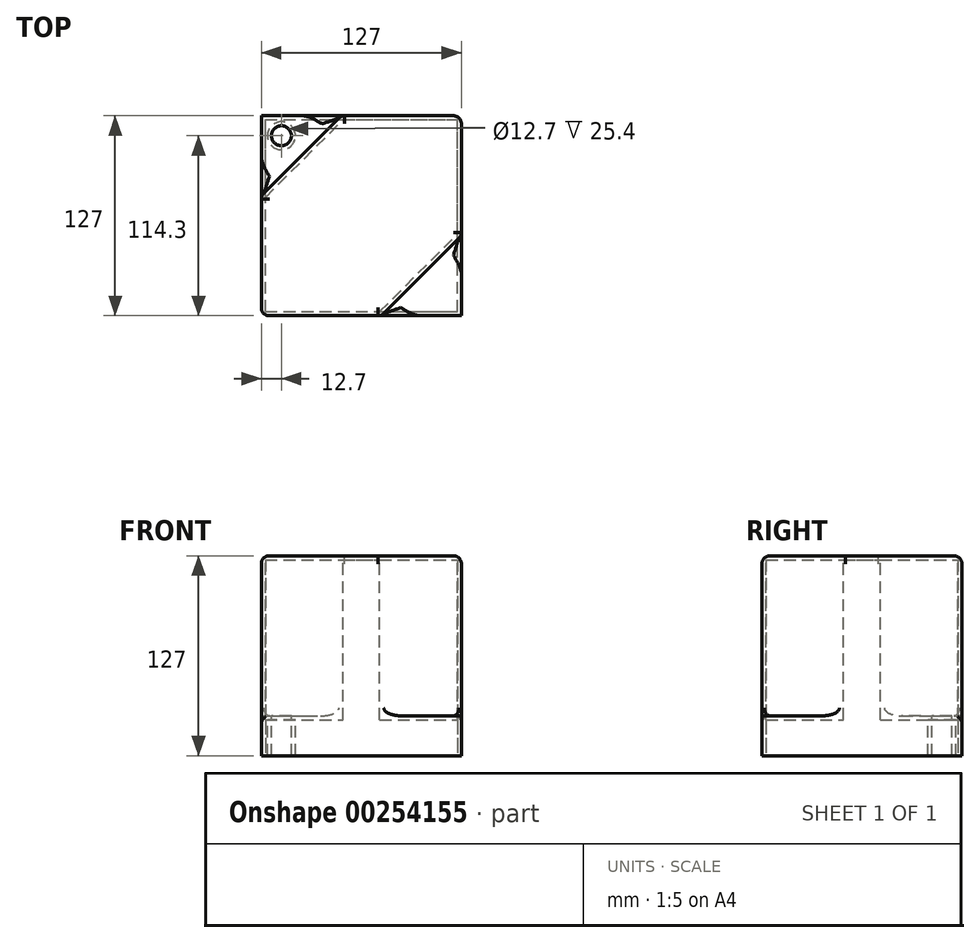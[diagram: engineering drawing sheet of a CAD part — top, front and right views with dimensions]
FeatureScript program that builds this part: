
annotation { "Feature Type Name" : "Feature", "Feature Type Description" : "" }
export const myFeature = defineFeature(function(context is Context, id is Id, definition is map)
    precondition{}
    {
        {
            var Q0;
            Q0=qCreatedBy(makeId("Top.planeOp"),FACE);
            var sketch = newSketch(context, id + "F0", { "sketchPlane" : qUnion([Q0])});
            skLineSegment(sketch, "E0.bottom", {"start": v(-63.5, -63.5) * mm, "end": v(63.5, -63.5) * mm});
            skLineSegment(sketch, "E0.top", {"start": v(-63.5, 63.5) * mm, "end": v(63.5, 63.5) * mm});
            skLineSegment(sketch, "E0.left", {"start": v(-63.5, -63.5) * mm, "end": v(-63.5, 63.5) * mm});
            skLineSegment(sketch, "E0.right", {"start": v(63.5, -63.5) * mm, "end": v(63.5, 63.5) * mm});
            skPoint(sketch, "E0.middle", {"position": v(0, 0) * mm});
            skLineSegment(sketch, "E1", {"start": v(63.5, 63.5) * mm, "end": v(-63.5, -63.5) * mm, "construction": true});
            skLineSegment(sketch, "E2", {"start": v(-63.5, 63.5) * mm, "end": v(-63.5, 12.7) * mm});
            skLineSegment(sketch, "E3", {"start": v(-12.7, 63.5) * mm, "end": v(-63.5, 63.5) * mm});
            skLineSegment(sketch, "E4.MirrorCS", {"start": v(63.5, -12.7) * mm, "end": v(63.5, -63.5) * mm});
            skLineSegment(sketch, "E5.MirrorCS", {"start": v(63.5, -63.5) * mm, "end": v(12.7, -63.5) * mm});
            skSolve(sketch);
        }
        {
            var Q0;
            Q0=makeQuery(id+"F0.imprint","IMPRINT",FACE,{"disambiguationData":[TD([[makeQuery(id+"F0.imprint","IMPRINT",EDGE,{"derivedFrom":sQuery(id+"F0.wireOp",EDGE,"E0.top")}),-1.0]])]});
            extrude(context, id + "F1", {"entities" : qUnion([Q0]), "depth" : 127 * mm});
        }
        {
            var Q0;
            Q0=makeQuery(id+"F1.opExtrude","CAP_FACE",FACE,{"disambiguationData":[OSD([sQuery(id+"F0.wireOp",EDGE,"E0.top"),sQuery(id+"F0.wireOp",EDGE,"E0.left"),sQuery(id+"F0.wireOp",EDGE,"E2"),sQuery(id+"F0.wireOp",EDGE,"E3"),sQuery(id+"F0.wireOp",EDGE,"E0.right"),sQuery(id+"F0.wireOp",EDGE,"E0.bottom"),sQuery(id+"F0.wireOp",EDGE,"E4.MirrorCS"),sQuery(id+"F0.wireOp",EDGE,"E5.MirrorCS")])],"isStart":false});
            var sketch = newSketch(context, id + "F2", { "sketchPlane" : qUnion([Q0])});
            skLineSegment(sketch, "E6", {"start": v(-63.5, 63.5) * mm, "end": v(-63.5, 12.7) * mm});
            skLineSegment(sketch, "E7", {"start": v(-63.5, 12.7) * mm, "end": v(-12.7, 63.5) * mm});
            skLineSegment(sketch, "E8", {"start": v(-12.7, 63.5) * mm, "end": v(-63.5, 63.5) * mm});
            skLineSegment(sketch, "E9", {"start": v(63.5, 63.5) * mm, "end": v(-63.5, -63.5) * mm, "construction": true});
            skLineSegment(sketch, "E10.MirrorCS", {"start": v(12.7, -63.5) * mm, "end": v(63.5, -12.7) * mm});
            skLineSegment(sketch, "E11.MirrorCS", {"start": v(63.5, -12.7) * mm, "end": v(63.5, -63.5) * mm});
            skLineSegment(sketch, "E12.MirrorCS", {"start": v(63.5, -63.5) * mm, "end": v(12.7, -63.5) * mm});
            skSolve(sketch);
        }
        {
            var Q0;
            Q0=makeQuery(id+"F2.imprint","IMPRINT",FACE,{"disambiguationData":[TD([[makeQuery(id+"F2.imprint","IMPRINT",EDGE,{"derivedFrom":sQuery(id+"F2.wireOp",EDGE,"E6")}),-1.0]])]});
            var Q1;
            Q1=makeQuery(id+"F2.imprint","IMPRINT",FACE,{"disambiguationData":[TD([[makeQuery(id+"F2.imprint","IMPRINT",EDGE,{"derivedFrom":sQuery(id+"F2.wireOp",EDGE,"E10.MirrorCS")}),-1.0]])]});
            extrude(context, id + "F3", {"entities" : qUnion([Q0, Q1]), "operationType" : NewBodyOperationType.REMOVE, "oppositeDirection" : true, "depth" : 101.6 * mm});
        }
        {
            var Q0;
            Q0=makeQuery(id+"F3.boolean.opBoolean","COPY",FACE,{"derivedFrom":makeQuery(id+"F3.opExtrude","CAP_FACE",FACE,{"disambiguationData":[OSD([sQuery(id+"F2.wireOp",EDGE,"E6"),sQuery(id+"F2.wireOp",EDGE,"E7"),sQuery(id+"F2.wireOp",EDGE,"E8")])],"isStart":false})});
            var sketch = newSketch(context, id + "F4", { "sketchPlane" : qUnion([Q0])});
            skCircle(sketch, "E13", {"center": v(-50.8, 50.8) * mm, "radius": 6.35 * mm});
            skLineSegment(sketch, "E14", {"start": v(63.28, 63.28) * mm, "end": v(-63, -63) * mm, "construction": true});
            skCircle(sketch, "E15.MirrorC", {"center": v(50.8, -50.8) * mm, "radius": 6.35 * mm});
            skSolve(sketch);
        }
        {
            var Q0;
            Q0=makeQuery(id+"F4.imprint","IMPRINT",FACE,{"disambiguationData":[TD([[makeQuery(id+"F4.imprint","IMPRINT",EDGE,{"derivedFrom":sQuery(id+"F4.wireOp",EDGE,"E13")}),1.0]])]});
            var Q1;
            Q1=makeQuery(id+"F4.imprint","IMPRINT",FACE,{"disambiguationData":[TD([[makeQuery(id+"F4.imprint","IMPRINT",EDGE,{"derivedFrom":sQuery(id+"F4.wireOp",EDGE,"E15.MirrorC")}),-1.0]])]});
            extrude(context, id + "F5", {"entities" : qUnion([Q0, Q1]), "operationType" : NewBodyOperationType.REMOVE, "oppositeDirection" : true, "depth" : 203.2 * mm});
        }
        {
            var Q0;
            Q0=makeQuery(id+"F1.opExtrude","CAP_FACE",FACE,{"disambiguationData":[OSD([sQuery(id+"F0.wireOp",EDGE,"E0.top"),sQuery(id+"F0.wireOp",EDGE,"E0.left"),sQuery(id+"F0.wireOp",EDGE,"E2"),sQuery(id+"F0.wireOp",EDGE,"E3"),sQuery(id+"F0.wireOp",EDGE,"E0.right"),sQuery(id+"F0.wireOp",EDGE,"E0.bottom"),sQuery(id+"F0.wireOp",EDGE,"E4.MirrorCS"),sQuery(id+"F0.wireOp",EDGE,"E5.MirrorCS")])],"isStart":true});
            shell(context, id + "F6", {"entities" : qUnion([Q0]), "thickness" : 2.54 * mm});
        }
        {
            var Q0;
            Q0=makeQuery(id+"F1.opExtrude","CAP_EDGE",EDGE,{"disambiguationData":[OSD([sQuery(id+"F0.wireOp",EDGE,"E0.left"),sQuery(id+"F0.wireOp",EDGE,"E2")])],"isStart":false});
            var Q1;
            Q1=makeQuery(id+"F1.opExtrude","SWEPT_EDGE",EDGE,{"disambiguationData":[OSD([sQuery(id+"F0.wireOp",EDGE,"E0.left"),sQuery(id+"F0.wireOp",EDGE,"E0.bottom")])]});
            var Q2;
            Q2=makeQuery(id+"F1.opExtrude","CAP_EDGE",EDGE,{"disambiguationData":[OSD([sQuery(id+"F0.wireOp",EDGE,"E0.bottom"),sQuery(id+"F0.wireOp",EDGE,"E5.MirrorCS")])],"isStart":false});
            var Q3;
            Q3=makeQuery(id+"F1.opExtrude","CAP_EDGE",EDGE,{"disambiguationData":[OSD([sQuery(id+"F0.wireOp",EDGE,"E0.right"),sQuery(id+"F0.wireOp",EDGE,"E4.MirrorCS")])],"isStart":false});
            var Q4;
            Q4=makeQuery(id+"F1.opExtrude","CAP_EDGE",EDGE,{"disambiguationData":[OSD([sQuery(id+"F0.wireOp",EDGE,"E0.top"),sQuery(id+"F0.wireOp",EDGE,"E3")])],"isStart":false});
            var Q5;
            Q5=makeQuery(id+"F1.opExtrude","SWEPT_EDGE",EDGE,{"disambiguationData":[OSD([sQuery(id+"F0.wireOp",EDGE,"E0.top"),sQuery(id+"F0.wireOp",EDGE,"E0.right")])]});
            fillet(context, id + "F7", {"entities" : qUnion([Q0, Q1, Q2, Q3, Q4, Q5]), "radius" : 5.08 * mm, "tangentPropagation" : true, "allowEdgeOverflow" : false});
        }
        {
            var Q0;
            Q0=makeQuery(id+"F3.boolean.opBoolean","COPY",FACE,{"derivedFrom":makeQuery(id+"F3.opExtrude","SWEPT_FACE",FACE,{"disambiguationData":[OSD([sQuery(id+"F2.wireOp",EDGE,"E10.MirrorCS")])]})});
            var Q1;
            Q1=makeQuery(id+"F3.boolean.opBoolean","COPY",FACE,{"derivedFrom":makeQuery(id+"F3.opExtrude","SWEPT_FACE",FACE,{"disambiguationData":[OSD([sQuery(id+"F2.wireOp",EDGE,"E7")])]})});
            var Q2;
            Q2=makeQuery(id+"F1.opExtrude","SWEPT_EDGE",EDGE,{"disambiguationData":[OSD([sQuery(id+"F0.wireOp",EDGE,"E2"),sQuery(id+"F0.wireOp",EDGE,"E3")])]});
            var Q3;
            Q3=makeQuery(id+"F1.opExtrude","SWEPT_EDGE",EDGE,{"disambiguationData":[OSD([sQuery(id+"F0.wireOp",EDGE,"E4.MirrorCS"),sQuery(id+"F0.wireOp",EDGE,"E5.MirrorCS")])]});
            fillet(context, id + "F8", {"entities" : qUnion([Q0, Q1, Q2, Q3]), "radius" : 5.08 * mm, "tangentPropagation" : true, "allowEdgeOverflow" : false});
        }
    });
